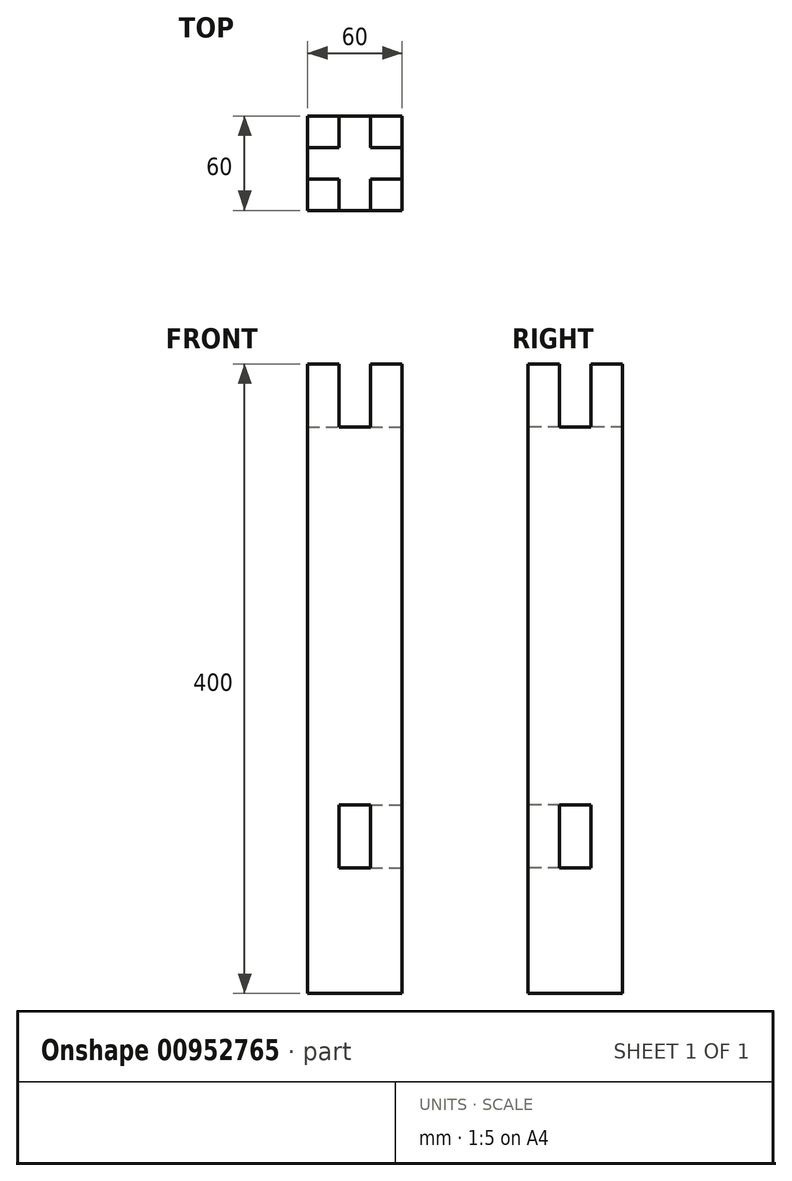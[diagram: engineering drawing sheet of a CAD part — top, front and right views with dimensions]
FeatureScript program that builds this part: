
annotation { "Feature Type Name" : "Feature", "Feature Type Description" : "" }
export const myFeature = defineFeature(function(context is Context, id is Id, definition is map)
    precondition{}
    {
        {
            var Q0;
            Q0=qCreatedBy(makeId("Top.planeOp"),FACE);
            var sketch = newSketch(context, id + "F0", { "sketchPlane" : qUnion([Q0])});
            skLineSegment(sketch, "E0.bottom", {"start": v(-62.33, 10.75) * mm, "end": v(-2.33, 10.75) * mm});
            skLineSegment(sketch, "E0.top", {"start": v(-62.33, -49.25) * mm, "end": v(-2.33, -49.25) * mm});
            skLineSegment(sketch, "E0.left", {"start": v(-62.33, 10.75) * mm, "end": v(-62.33, -49.25) * mm});
            skLineSegment(sketch, "E0.right", {"start": v(-2.33, 10.75) * mm, "end": v(-2.33, -49.25) * mm});
            skSolve(sketch);
        }
        {
            var Q0;
            Q0=makeQuery(id+"F0.imprint","IMPRINT",FACE,{"disambiguationData":[TD([[makeQuery(id+"F0.imprint","IMPRINT",EDGE,{"derivedFrom":sQuery(id+"F0.wireOp",EDGE,"E0.bottom")}),-1.0]])]});
            extrude(context, id + "F1", {"entities" : qUnion([Q0]), "oppositeDirection" : true, "depth" : 400 * mm, "offsetDistance" : 25 * mm});
        }
        {
            var Q0;
            Q0=makeQuery(id+"F1.opExtrude","CAP_FACE",FACE,{"disambiguationData":[OSD([sQuery(id+"F0.wireOp",EDGE,"E0.bottom"),sQuery(id+"F0.wireOp",EDGE,"E0.top"),sQuery(id+"F0.wireOp",EDGE,"E0.left"),sQuery(id+"F0.wireOp",EDGE,"E0.right")])],"isStart":true});
            var sketch = newSketch(context, id + "F2", { "sketchPlane" : qUnion([Q0])});
            skLineSegment(sketch, "E1", {"start": v(-62.33, -9.25) * mm, "end": v(-2.33, -9.25) * mm});
            skLineSegment(sketch, "E2", {"start": v(-62.33, -29.25) * mm, "end": v(-2.33, -29.25) * mm});
            skLineSegment(sketch, "E3", {"start": v(-42.33, 10.75) * mm, "end": v(-42.33, -49.25) * mm});
            skLineSegment(sketch, "E4", {"start": v(-22.33, 10.75) * mm, "end": v(-22.33, -49.25) * mm});
            skSolve(sketch);
        }
        {
            var Q0;
            {var subQ0=sQuery(id+"F2.wireOp",EDGE,"E3");var subQ1=sQuery(id+"F2.wireOp",EDGE,"E1");var subQ2=makeQuery(id+"F2.imprint","INTERSECT",VERTEX,{"derivedFrom":[subQ1,subQ0]});Q0=makeQuery(id+"F2.imprint","IMPRINT",FACE,{"disambiguationData":[TD([[makeQuery(id+"F2.imprint","IMPRINT",EDGE,{"disambiguationData":[TD([[subQ2,-1.0]])],"derivedFrom":subQ1}),-1.0]])]});}
            var Q1;
            {var subQ0=sQuery(id+"F2.wireOp",EDGE,"E1");var subQ1=makeQuery(id+"F1.opExtrude","CAP_EDGE",EDGE,{"disambiguationData":[OSD([sQuery(id+"F0.wireOp",EDGE,"E0.left")])],"isStart":true});var subQ2=makeQuery(id+"F2.imprint","INTERSECT",VERTEX,{"derivedFrom":[subQ1,subQ0]});Q1=makeQuery(id+"F2.imprint","IMPRINT",FACE,{"disambiguationData":[TD([[makeQuery(id+"F2.imprint","IMPRINT",EDGE,{"disambiguationData":[TD([[subQ2,-1.0]])],"derivedFrom":subQ0}),-1.0]])]});}
            var Q2;
            {var subQ0=sQuery(id+"F2.wireOp",EDGE,"E3");var subQ1=sQuery(id+"F2.wireOp",EDGE,"E1");var subQ2=makeQuery(id+"F2.imprint","INTERSECT",VERTEX,{"derivedFrom":[subQ1,subQ0]});Q2=makeQuery(id+"F2.imprint","IMPRINT",FACE,{"disambiguationData":[TD([[makeQuery(id+"F2.imprint","IMPRINT",EDGE,{"disambiguationData":[TD([[subQ2,-1.0]])],"derivedFrom":subQ1}),1.0]])]});}
            var Q3;
            {var subQ0=sQuery(id+"F2.wireOp",EDGE,"E1");var subQ1=makeQuery(id+"F1.opExtrude","CAP_EDGE",EDGE,{"disambiguationData":[OSD([sQuery(id+"F0.wireOp",EDGE,"E0.right")])],"isStart":true});var subQ2=makeQuery(id+"F2.imprint","INTERSECT",VERTEX,{"derivedFrom":[subQ1,subQ0]});Q3=makeQuery(id+"F2.imprint","IMPRINT",FACE,{"disambiguationData":[TD([[makeQuery(id+"F2.imprint","IMPRINT",EDGE,{"disambiguationData":[TD([[subQ2,1.0]])],"derivedFrom":subQ0}),-1.0]])]});}
            var Q4;
            {var subQ0=sQuery(id+"F2.wireOp",EDGE,"E3");var subQ1=sQuery(id+"F2.wireOp",EDGE,"E2");var subQ2=makeQuery(id+"F2.imprint","INTERSECT",VERTEX,{"derivedFrom":[subQ1,subQ0]});Q4=makeQuery(id+"F2.imprint","IMPRINT",FACE,{"disambiguationData":[TD([[makeQuery(id+"F2.imprint","IMPRINT",EDGE,{"disambiguationData":[TD([[subQ2,-1.0]])],"derivedFrom":subQ1}),-1.0]])]});}
            extrude(context, id + "F3", {"entities" : qUnion([Q0, Q1, Q2, Q3, Q4]), "operationType" : NewBodyOperationType.REMOVE, "oppositeDirection" : true, "depth" : 40 * mm, "offsetDistance" : 25 * mm});
        }
        {
            var Q0;
            Q0=makeQuery(id+"F1.opExtrude","SWEPT_FACE",FACE,{"disambiguationData":[OSD([sQuery(id+"F0.wireOp",EDGE,"E0.top")])]});
            var sketch = newSketch(context, id + "F4", { "sketchPlane" : qUnion([Q0])});
            skLineSegment(sketch, "E5.bottom", {"start": v(-42.33, -280) * mm, "end": v(-22.33, -280) * mm});
            skLineSegment(sketch, "E5.top", {"start": v(-42.33, -320) * mm, "end": v(-22.33, -320) * mm});
            skLineSegment(sketch, "E5.left", {"start": v(-42.33, -280) * mm, "end": v(-42.33, -320) * mm});
            skLineSegment(sketch, "E5.right", {"start": v(-22.33, -280) * mm, "end": v(-22.33, -320) * mm});
            skSolve(sketch);
        }
        {
            var Q0;
            Q0=makeQuery(id+"F4.imprint","IMPRINT",FACE,{"disambiguationData":[TD([[makeQuery(id+"F4.imprint","IMPRINT",EDGE,{"derivedFrom":sQuery(id+"F4.wireOp",EDGE,"E5.bottom")}),-1.0]])]});
            extrude(context, id + "F5", {"entities" : qUnion([Q0]), "operationType" : NewBodyOperationType.REMOVE, "oppositeDirection" : true, "depth" : 40 * mm, "offsetDistance" : 25 * mm});
        }
        {
            var Q0;
            Q0=makeQuery(id+"F1.opExtrude","SWEPT_FACE",FACE,{"disambiguationData":[OSD([sQuery(id+"F0.wireOp",EDGE,"E0.right")])]});
            var sketch = newSketch(context, id + "F6", { "sketchPlane" : qUnion([Q0])});
            skLineSegment(sketch, "E6.bottom", {"start": v(-29.25, -280) * mm, "end": v(-9.25, -280) * mm});
            skLineSegment(sketch, "E6.top", {"start": v(-29.25, -320) * mm, "end": v(-9.25, -320) * mm});
            skLineSegment(sketch, "E6.left", {"start": v(-29.25, -280) * mm, "end": v(-29.25, -320) * mm});
            skLineSegment(sketch, "E6.right", {"start": v(-9.25, -280) * mm, "end": v(-9.25, -320) * mm});
            skSolve(sketch);
        }
        {
            var Q0;
            Q0=makeQuery(id+"F6.imprint","IMPRINT",FACE,{"disambiguationData":[TD([[makeQuery(id+"F6.imprint","IMPRINT",EDGE,{"derivedFrom":sQuery(id+"F6.wireOp",EDGE,"E6.bottom")}),-1.0]])]});
            extrude(context, id + "F7", {"entities" : qUnion([Q0]), "operationType" : NewBodyOperationType.REMOVE, "oppositeDirection" : true, "depth" : 40 * mm, "offsetDistance" : 25 * mm});
        }
    });
